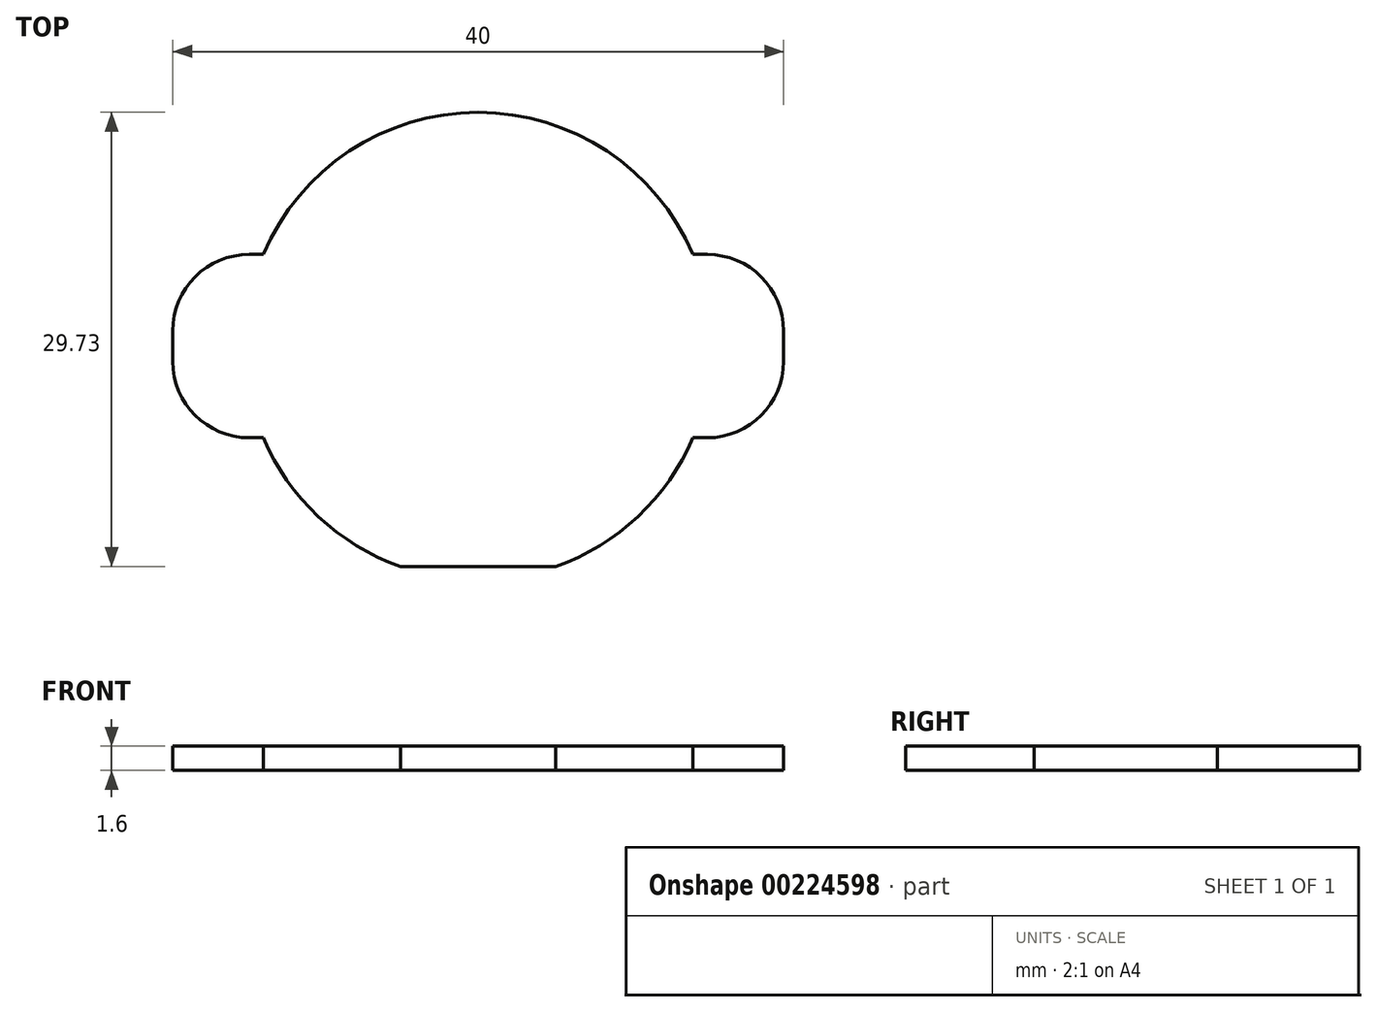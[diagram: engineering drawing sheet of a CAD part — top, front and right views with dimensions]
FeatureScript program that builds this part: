
annotation { "Feature Type Name" : "Feature", "Feature Type Description" : "" }
export const myFeature = defineFeature(function(context is Context, id is Id, definition is map)
    precondition{}
    {
        {
            var Q0;
            Q0=qCreatedBy(makeId("Top.planeOp"),FACE);
            var sketch = newSketch(context, id + "F0", { "sketchPlane" : qUnion([Q0])});
            skLineSegment(sketch, "E0", {"start": v(0, -8.76) * mm, "end": v(5.08, -8.76) * mm, "construction": true});
            skLineSegment(sketch, "E1", {"start": v(5.08, -8.76) * mm, "end": v(5.08, -14.43) * mm, "construction": true});
            skLineSegment(sketch, "E2", {"start": v(5.08, -14.43) * mm, "end": v(-5.08, -14.43) * mm});
            skArc(sketch, "E3", {"start": v(5.08, -14.43) * mm, "mid": v(10.46, -11.16) * mm, "end": v(14.07, -6) * mm});
            skLineSegment(sketch, "E4.left", {"start": v(20, -1) * mm, "end": v(20, 1) * mm});
            skLineSegment(sketch, "E4.right", {"start": v(-20, -1) * mm, "end": v(-20, 1) * mm});
            skPoint(sketch, "E5.visualSharp", {"position": v(20, 6) * mm});
            skArc(sketch, "E5.filletArc", {"start": v(20, 1) * mm, "mid": v(18.54, 4.54) * mm, "end": v(15, 6) * mm});
            skPoint(sketch, "E6.visualSharp", {"position": v(20, -6) * mm});
            skArc(sketch, "E6.filletArc", {"start": v(15, -6) * mm, "mid": v(18.54, -4.54) * mm, "end": v(20, -1) * mm});
            skPoint(sketch, "E7.visualSharp", {"position": v(-20, -6) * mm});
            skArc(sketch, "E7.filletArc", {"start": v(-20, -1) * mm, "mid": v(-18.54, -4.54) * mm, "end": v(-15, -6) * mm});
            skPoint(sketch, "E8.visualSharp", {"position": v(-20, 6) * mm});
            skArc(sketch, "E8.filletArc", {"start": v(-15, 6) * mm, "mid": v(-18.54, 4.54) * mm, "end": v(-20, 1) * mm});
            skArc(sketch, "E9", {"start": v(-14.07, -6) * mm, "mid": v(-10.46, -11.16) * mm, "end": v(-5.08, -14.43) * mm});
            skArc(sketch, "E10", {"start": v(14.07, 6) * mm, "mid": v(0, 15.3) * mm, "end": v(-14.07, 6) * mm});
            skLineSegment(sketch, "E11", {"start": v(-15, 6) * mm, "end": v(-14.07, 6) * mm});
            skLineSegment(sketch, "E12", {"start": v(14.07, 6) * mm, "end": v(15, 6) * mm});
            skLineSegment(sketch, "E13", {"start": v(15, -6) * mm, "end": v(14.07, -6) * mm});
            skLineSegment(sketch, "E14", {"start": v(-15, -6) * mm, "end": v(-14.07, -6) * mm});
            skSolve(sketch);
        }
        {
            var Q0;
            Q0 = qSketchRegion(id + "F0", true);
            extrude(context, id + "F1", {"entities" : qUnion([Q0]), "depth" : 1.6 * mm, "offsetDistance" : 25 * mm});
        }
    });
